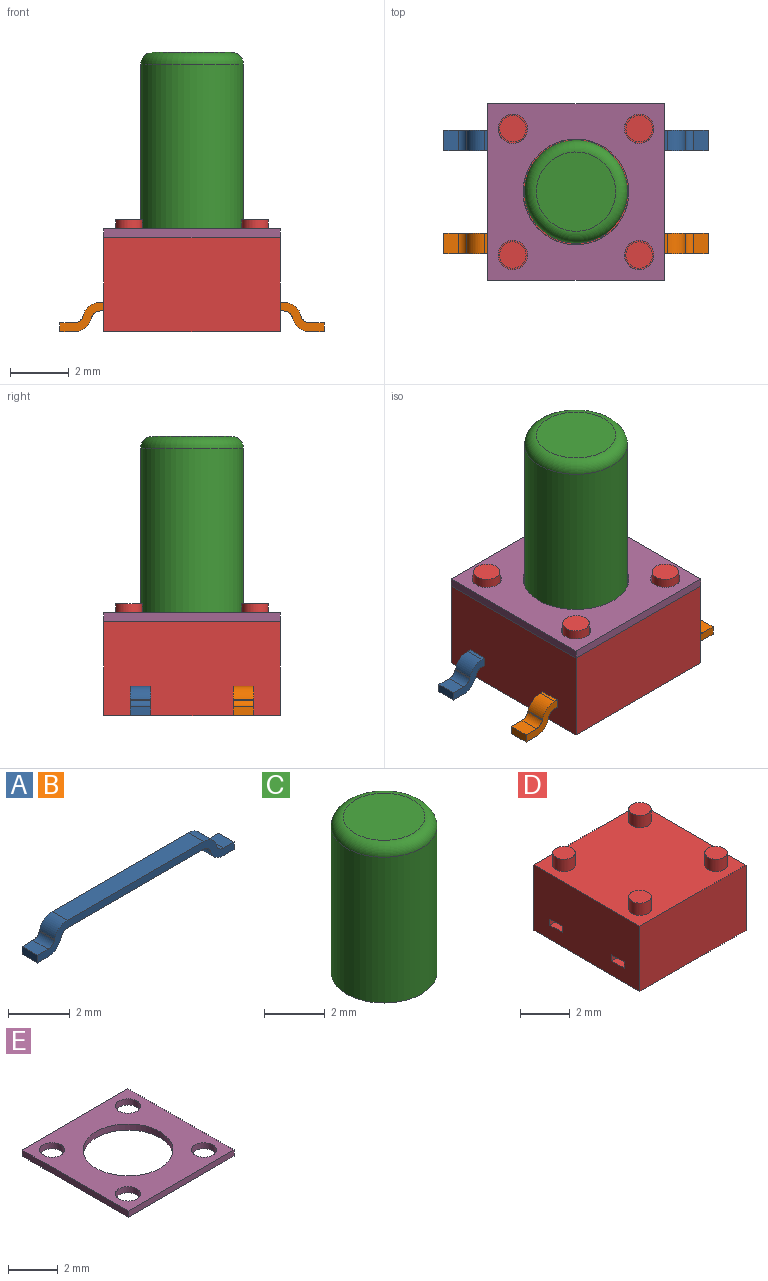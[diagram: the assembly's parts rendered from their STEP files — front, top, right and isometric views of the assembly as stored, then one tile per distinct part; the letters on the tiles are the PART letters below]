
ASSEMBLY  parts=5 mates=4
PART A: 22 faces, bbox 9x0.7x1 mm
  f0: plane 0.7x0.5mm, normal (0,0,1), area 0.3mm2, adj f1,f19,f20,f21
  f1: cylinder r=0.3mm len=0.7mm, axis (0,1,0), area 0.3mm2, adj f0,f2,f20,f21
  f2: plane 0.7x0.04mm, normal (-0.98,0,-0.17), area 0mm2, adj f1,f3,f20,f21
  f3: cylinder r=0.6mm len=0.7mm, axis (0,1,0), area 0.6mm2, adj f2,f4,f20,f21
  f4: plane 6.25x0.7mm, normal (0,0,1), area 4.4mm2, adj f3,f5,f20,f21
  f5: cylinder r=0.6mm len=0.7mm, axis (0,1,0), area 0.6mm2, adj f4,f6,f20,f21
  f6: plane 0.7x0.04mm, normal (0.98,0,-0.17), area 0mm2, adj f5,f7,f20,f21
  f7: cylinder r=0.3mm len=0.7mm, axis (0,1,0), area 0.3mm2, adj f6,f8,f20,f21
  f8: plane 0.7x0.5mm, normal (0,0,1), area 0.3mm2, adj f7,f9,f20,f21
  f9: plane 0.7x0.3mm, normal (-1,0,0), area 0.2mm2, adj f8,f10,f20,f21
  f10: plane 0.7x0.5mm, normal (0,0,-1), area 0.3mm2, adj f9,f11,f20,f21
  f11: cylinder r=0.6mm len=0.7mm, axis (0,1,0), area 0.6mm2, adj f10,f12,f20,f21
  f12: plane 0.7x0.04mm, normal (-0.98,0,0.17), area 0mm2, adj f11,f13,f20,f21
  f13: cylinder r=0.3mm len=0.7mm, axis (0,1,0), area 0.3mm2, adj f12,f14,f20,f21
  f14: plane 6.25x0.7mm, normal (0,0,-1), area 4.4mm2, adj f13,f15,f20,f21
  f15: cylinder r=0.3mm len=0.7mm, axis (0,1,0), area 0.3mm2, adj f14,f16,f20,f21
  f16: plane 0.7x0.04mm, normal (0.98,0,0.17), area 0mm2, adj f15,f17,f20,f21
  f17: cylinder r=0.6mm len=0.7mm, axis (0,1,0), area 0.6mm2, adj f16,f18,f20,f21
  f18: plane 0.7x0.5mm, normal (0,0,-1), area 0.3mm2, adj f17,f19,f20,f21
  f19: plane 0.7x0.3mm, normal (1,0,0), area 0.2mm2, adj f0,f18,f20,f21
  f20: plane 9x1mm, normal (0,-1,0), area 2.9mm2, adj f0,f1,f2,f3,f4,f5,f6,f7
  f21: plane 9x1mm, normal (0,1,0), area 2.9mm2, adj f0,f1,f2,f3,f4,f5,f6,f7
PART B: same geometry as A
PART C: 4 faces, bbox 3.8x3.8x6.3 mm
  f0: cylinder r=1.75mm len=5.9mm, axis (0,0,-1), area 64.9mm2, adj f2,f3
  f1: plane 2.7x2.7mm, normal (0,0,1), area 5.7mm2, adj f3
  f2: plane 3.5x3.5mm, normal (0,0,-1), area 9.6mm2, adj f0
  f3: torus R=1.35mm, axis (0,0,1), area 6.3mm2, adj f0,f1
PART D: 22 faces, bbox 6x6x3.8 mm
  f0: plane 6x3.2mm, normal (-1,0,0), area 18.8mm2, adj f1,f3,f4,f5,f14,f15,f16,f17
  f1: plane 6x3.2mm, normal (0,-1,0), area 19.2mm2, adj f0,f2,f4,f5
  f2: plane 6x3.2mm, normal (1,0,0), area 18.8mm2, adj f1,f3,f4,f5,f14,f15,f16,f17
  f3: plane 6x3.2mm, normal (0,1,0), area 19.2mm2, adj f0,f2,f4,f5
  f4: plane 6x6mm, normal (0,0,1), area 33.5mm2, adj f0,f1,f2,f3,f6,f8,f10,f12
  f5: plane 6x6mm, normal (0,0,-1), area 36mm2, adj f0,f1,f2,f3
  f6: cylinder r=0.45mm len=0.9mm, axis (0,0,-1), area 1.7mm2, adj f4,f7
  f7: plane 0.9x0.9mm, normal (0,0,1), area 0.6mm2, adj f6
  f8: cylinder r=0.45mm len=0.9mm, axis (0,0,-1), area 1.7mm2, adj f4,f9
  f9: plane 0.9x0.9mm, normal (0,0,1), area 0.6mm2, adj f8
  f10: cylinder r=0.45mm len=0.9mm, axis (0,0,-1), area 1.7mm2, adj f4,f11
  f11: plane 0.9x0.9mm, normal (0,0,1), area 0.6mm2, adj f10
  f12: cylinder r=0.45mm len=0.9mm, axis (0,0,-1), area 1.7mm2, adj f4,f13
  f13: plane 0.9x0.9mm, normal (0,0,1), area 0.6mm2, adj f12
  f14: plane 6x0.3mm, normal (0,1,0), area 1.8mm2, adj f0,f2,f15,f17
  f15: plane 6x0.7mm, normal (0,0,1), area 4.2mm2, adj f0,f2,f14,f16
  f16: plane 6x0.3mm, normal (0,-1,0), area 1.8mm2, adj f0,f2,f15,f17
  f17: plane 6x0.7mm, normal (0,0,-1), area 4.2mm2, adj f0,f2,f14,f16
  f18: plane 6x0.3mm, normal (0,1,0), area 1.8mm2, adj f0,f2,f19,f21
  f19: plane 6x0.7mm, normal (0,0,1), area 4.2mm2, adj f0,f2,f18,f20
  f20: plane 6x0.3mm, normal (0,-1,0), area 1.8mm2, adj f0,f2,f19,f21
  f21: plane 6x0.7mm, normal (0,0,-1), area 4.2mm2, adj f0,f2,f18,f20
PART E: 11 faces, bbox 6x6x0.3 mm
  f0: plane 6x0.3mm, normal (-1,0,0), area 1.8mm2, adj f1,f3,f4,f5
  f1: plane 6x0.3mm, normal (0,-1,0), area 1.8mm2, adj f0,f2,f4,f5
  f2: plane 6x0.3mm, normal (1,0,0), area 1.8mm2, adj f1,f3,f4,f5
  f3: plane 6x0.3mm, normal (0,1,0), area 1.8mm2, adj f0,f2,f4,f5
  f4: plane 6x6mm, normal (0,0,1), area 22.7mm2, adj f0,f1,f2,f3,f6,f7,f8,f9
  f5: plane 6x6mm, normal (0,0,-1), area 22.7mm2, adj f0,f1,f2,f3,f6,f7,f8,f9
  f6: cylinder r=0.5mm len=1mm, axis (0,0,1), area 0.9mm2, adj f4,f5
  f7: cylinder r=0.5mm len=1mm, axis (0,0,1), area 0.9mm2, adj f4,f5
  f8: cylinder r=1.8mm len=3.6mm, axis (0,0,1), area 3.4mm2, adj f4,f5
  f9: cylinder r=0.5mm len=1mm, axis (0,0,1), area 0.9mm2, adj f4,f5
  f10: cylinder r=0.5mm len=1mm, axis (0,0,1), area 0.9mm2, adj f4,f5
PLACE A t=(-1.11,1.85,2.14)mm
PLACE B t=(-1.11,-1.65,2.14)mm
PLACE C t=(16.93,22.01,2.31)mm
PLACE D t=(-14.33,-31.77,-0.89)mm fixed
PLACE E t=(11.99,-30.84,2.31)mm
MATE fastened D.f17 <-> A.f4  axis (0,0,-1) through (-1.11,1.85,0.11)mm
MATE fastened D.f21 <-> B.f4  axis (0,0,-1) through (-1.11,-1.65,0.11)mm
MATE fastened C.f0 <-> D.f4  axis (0,0,-1) through (-1.11,0.1,2.31)mm
MATE fastened E.f8 <-> D.f4  axis (0,0,-1) through (-1.11,0.1,2.31)mm
